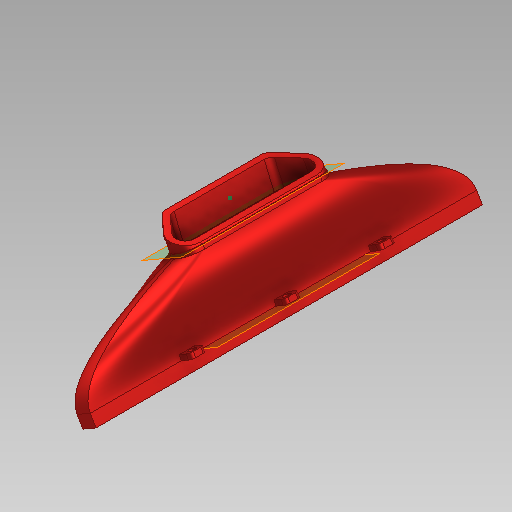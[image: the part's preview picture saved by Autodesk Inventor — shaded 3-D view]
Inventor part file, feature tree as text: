
AUTODESK INVENTOR PART (.ipt)
format: ipt  version: 2020 (Build 240168000, 168)  size: 824,832 bytes
history: native  units: in
note: dims shown in document units (in); Inventor stores cm internally (conversion verified against a paired STEP export)
features: sketch x13, extrude x9, fillet x5, other x4, loft x3, plane x2, mirror x1, pattern_linear x1
ambient origin geometry x8: Origin, YZ Plane, XZ Plane, XY Plane, X Axis, Y Axis, Z Axis, Center Point
bodies: Solid1 (feature_tree)
feature tree (38):
  extrude  "Extrusion1"  Depth=0.3543in
  fillet  "Fillet1"  Radius=0.3543in
  fillet  "Fillet2"  Radius=1.0236in
  plane  "Work Plane1"
  extrude  "Extrusion2"  Depth=1.0236in
  fillet  "Fillet3"  Radius=1.6555in
  fillet  "Fillet4"  Radius=0.4724in
  loft  "Loft1"
  mirror  "Mirror4"
  extrude  "Extrusion3"  Depth=0.1181in
  extrude  "Extrusion4"  Depth=0.1181in
  extrude  "Extrusion5"  TaperAngle=0.0deg  [1 undecoded]
  extrude  "Extrusion6"  Depth=0.0787in TaperAngle=0.0deg
  extrude  "Extrusion7"  Depth=0.315in
  plane  "Work Plane2"
  loft  "Loft4"
  loft  "Loft5"
  extrude  "Extrusion10"  Depth=0.0394in TaperAngle=0.0deg
  sketch  "Sketch13"  dims[d49=0.0394in d50=0.0in d51=0.0394in d52=0.0in]
  extrude  "Extrusion11"  Depth=1.378in
  fillet  "Fillet6"  Radius=0.0787in
  pattern_linear  "Rectangular Pattern1"  Spacing1=0.0787in  [1 undecoded]
  sketch  "Sketch15"  dims[d58=0.1575in d59=0.0787in d60=0.0787in d61=0.315in d90=0.0787in d91=0.0787in d93=0.0787in d94=7.874in d102=0.0in d103=90.0deg d106=0.1575in d107=7.874in d112=0.3937in d113=90.0deg d114=0.0in d115=90.0deg d116=0.0in d117=90.0deg d118=0.2362in d119=0.0in d120=3.937in d121=1.9685in d122=0.1575in d123=0.315in d124=0.315in d125=0.1181in d126=0.1575in d127=0.0984in d128=0.0in d129=0.0787in d130=1.1811in d132=1.9685in]
  sketch  "Sketch1"  dims[d0=0.3543in d1=0.3543in d2=0.3543in d3=1.0236in]
  sketch  "Sketch3"  dims[d4=90.0deg d5=1.0236in d7=1.6555in d9=0.4724in]
  other  "Edges1"
  other  "Edges2"
  sketch  "Sketch4"  dims[d10=0.9449in d17=0.0394in d18=0.0in]
  sketch  "Sketch5"  dims[d19=0.1969in d21=0.1181in]
  sketch  "Sketch6"  dims[d22=0.315in d23=0.1181in]
  sketch  "Sketch7"  dims[d24=30.0deg d35=0.0in]
  sketch  "Sketch8"  dims[d36=0.1181in d37=0.0787in d38=0.0in]
  sketch  "Sketch10"  dims[d39=0.1969in d40=0.315in]
  sketch  "Sketch11"  dims[d41=0.0in d42=90.0deg d43=0.0in d44=90.0deg]
  other  "Edges13"
  sketch  "Sketch12"  dims[d45=0.0787in d46=0.0in d47=0.0394in d48=0.0in]
  other  "Edges14"
  sketch  "Sketch14"  dims[d53=0.0394in d54=0.0in d55=1.378in d57=0.0787in]
note: 2 required parameter values undecoded (feature->parameter linkage not recoverable at this tier; creation-order binding heuristic only, values carry confidence <= 0.55)
